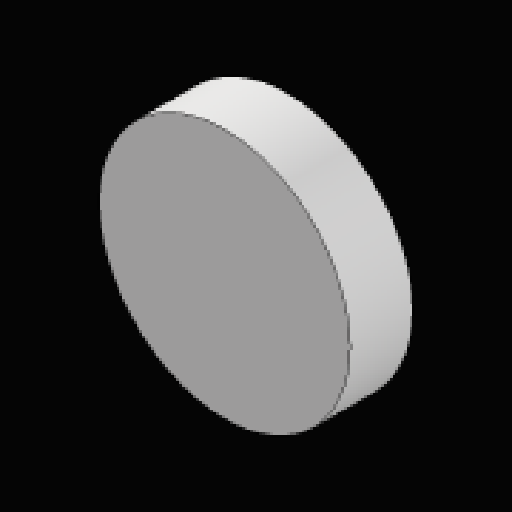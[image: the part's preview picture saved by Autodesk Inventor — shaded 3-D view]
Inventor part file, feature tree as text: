
AUTODESK INVENTOR PART (.ipt)
format: ipt  version: 2023.2 (Build 272271030, 271C)  size: 86,016 bytes
history: native  units: mm
features: extrude x1, sketch x1
ambient origin geometry x8: Origin, YZ Plane, XZ Plane, XY Plane, X Axis, Y Axis, Z Axis, Center Point
bodies: Solid1 (feature_tree)
feature tree (2):
  extrude  "Extrusion1"  Depth=5.0mm TaperAngle=0.0deg
  sketch  "Sketch1"  dims[d0=20.0mm d1=5.0mm d2=0.0mm]
